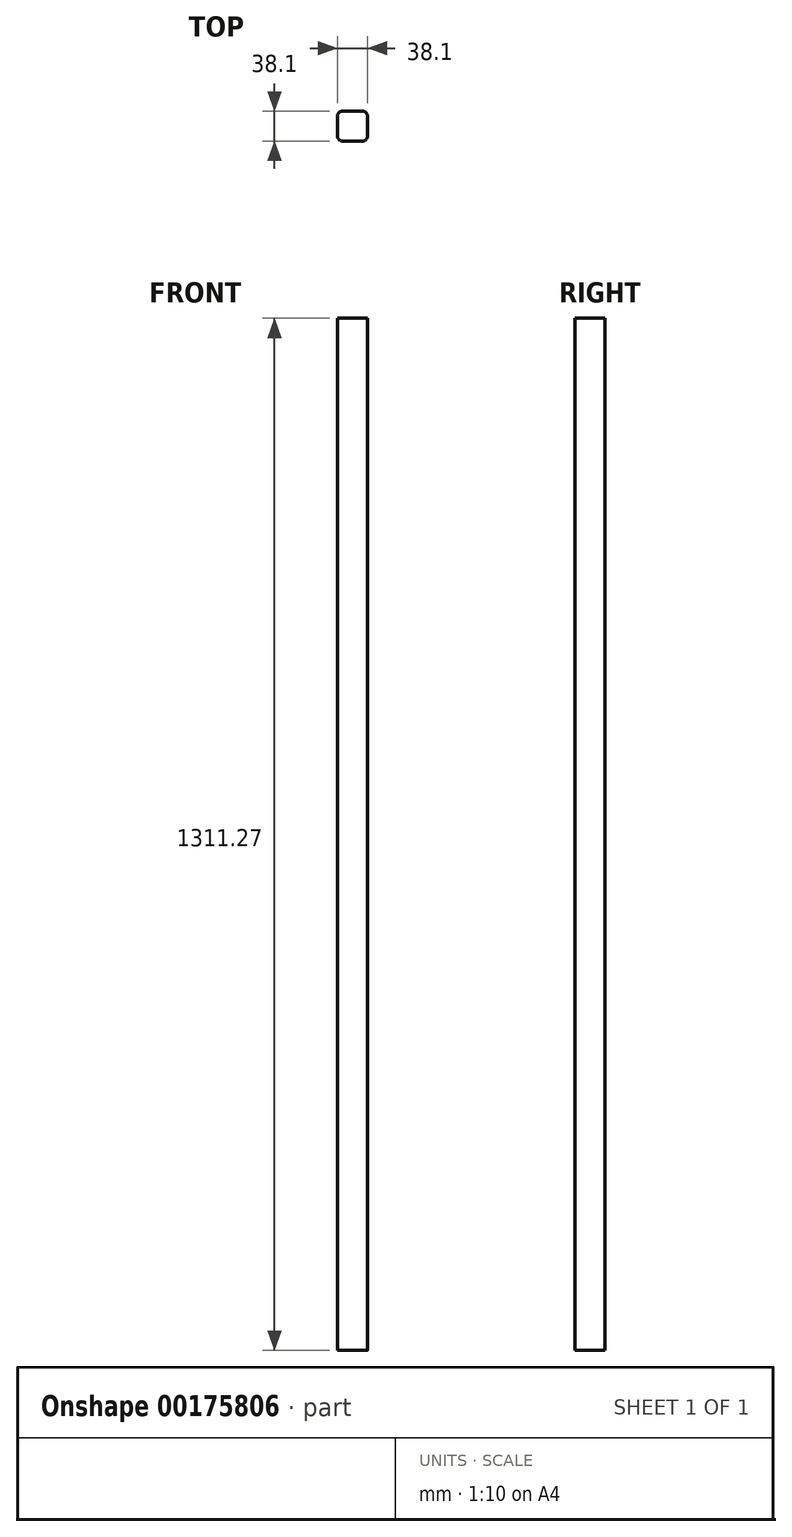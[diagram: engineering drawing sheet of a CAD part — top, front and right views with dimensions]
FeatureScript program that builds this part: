
annotation { "Feature Type Name" : "Feature", "Feature Type Description" : "" }
export const myFeature = defineFeature(function(context is Context, id is Id, definition is map)
    precondition{}
    {
        {
            var Q0;
            Q0=qCreatedBy(makeId("Top.planeOp"),FACE);
            var sketch = newSketch(context, id + "F0", { "sketchPlane" : qUnion([Q0])});
            skLineSegment(sketch, "E0.bottom", {"start": v(12.7, 19.05) * mm, "end": v(-12.7, 19.05) * mm});
            skLineSegment(sketch, "E0.top", {"start": v(12.7, -19.05) * mm, "end": v(-12.7, -19.05) * mm});
            skLineSegment(sketch, "E0.left", {"start": v(19.05, 12.7) * mm, "end": v(19.05, -12.7) * mm});
            skLineSegment(sketch, "E0.right", {"start": v(-19.05, 12.7) * mm, "end": v(-19.05, -12.7) * mm});
            skPoint(sketch, "E0.middle", {"position": v(0, 0) * mm});
            skPoint(sketch, "E1.visualSharp", {"position": v(-19.05, 19.05) * mm});
            skArc(sketch, "E1.filletArc", {"start": v(-12.7, 19.05) * mm, "mid": v(-17.2, 17.2) * mm, "end": v(-19.05, 12.7) * mm});
            skPoint(sketch, "E2.visualSharp", {"position": v(19.05, 19.05) * mm});
            skArc(sketch, "E2.filletArc", {"start": v(19.05, 12.7) * mm, "mid": v(17.2, 17.2) * mm, "end": v(12.7, 19.05) * mm});
            skPoint(sketch, "E3.visualSharp", {"position": v(19.05, -19.05) * mm});
            skArc(sketch, "E3.filletArc", {"start": v(12.7, -19.05) * mm, "mid": v(17.2, -17.2) * mm, "end": v(19.05, -12.7) * mm});
            skPoint(sketch, "E4.visualSharp", {"position": v(-19.05, -19.05) * mm});
            skArc(sketch, "E4.filletArc", {"start": v(-19.05, -12.7) * mm, "mid": v(-17.2, -17.2) * mm, "end": v(-12.7, -19.05) * mm});
            skSolve(sketch);
        }
        {
            var Q0;
            Q0=qSketchRegion(id+"F0",true);
            extrude(context, id + "F1", {"entities" : qUnion([Q0]), "depth" : 1311.27 * mm, "offsetDistance" : 25.4 * mm});
        }
    });
